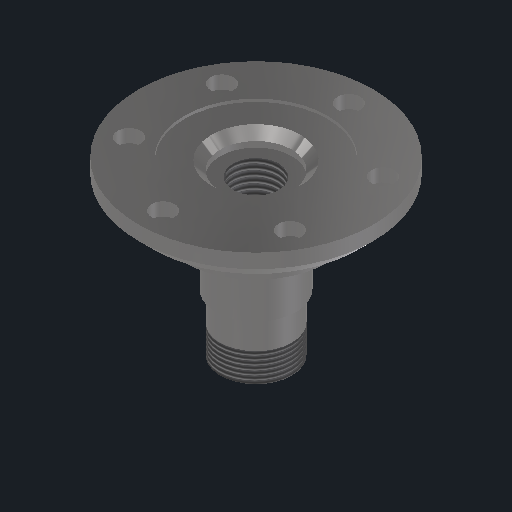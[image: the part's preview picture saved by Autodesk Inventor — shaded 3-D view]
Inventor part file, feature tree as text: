
AUTODESK INVENTOR PART (.ipt)
format: ipt  version: 2022 (Build 260153000, 153)  size: 221,184 bytes
history: native  units: mm
features: chamfer x4, sketch x3, other x3, thread x2, revolve x1, hole x1, extrude x1, reference x1, projected_geometry x1
ambient origin geometry x8: Origin, YZ Plane, XZ Plane, XY Plane, X Axis, Y Axis, Z Axis, Center Point
bodies: Solid1 (feature_tree)
feature tree (17):
  revolve  "Revolution1"  [1 undecoded]
  thread  "Thread1"  [1 undecoded]
  chamfer  "Chamfer1"  Distance=44.0mm
  chamfer  "Chamfer2"  Distance=25.0mm
  hole  "Hole1"  [1 undecoded]
  chamfer  "Chamfer4"  Distance=1.0mm
  extrude  "Extrusion1"  Depth=6.0mm
  chamfer  "Chamfer5"  Distance=5.0mm Angle=45.0deg
  thread  "Thread2"  [1 undecoded]
  sketch  "Sketch1"  dims[d3=28.0mm d4=50.0mm d7=360.0deg d8=44.0mm d9=0.0mm]
  sketch  "Sketch2"  dims[d10=16.0mm]
  reference  "Reference1"
  sketch  "Sketch3"  dims[d11=82.0mm d13=25.0mm d14=50.0mm d15=1.0mm d16=6.0mm d17=5.0mm d18=2.0mm d19=45.0deg d21=10.0mm d23=50.0mm d24=5.0mm d25=2.0mm d26=45.0deg d30=65.0mm d31=60.0mm d33=360.0deg d35=4.5mm d36=6.0mm d37=8.0mm d38=4.6mm d39=14.3117mm d40=12.0mm d41=20.594885mm d42=3.0mm d43=2.0mm d44=30.0deg d45=25.0mm d46=20.0mm d47=0.0mm d48=20.0mm d49=2.0mm d50=2.0mm d51=45.0deg d52=10.0mm d53=0.0mm d54=10.0mm d55=0.872665mm]
  projected_geometry  "Projected Loop1"
  other  "SistemaDeElevación.iam"
  other  "Bearing:2"
  other  "ISO 104 (Single Direction) 1 11 - 30 x 47 x 11:1"
note: 4 required parameter values undecoded (feature->parameter linkage not recoverable at this tier; creation-order binding heuristic only, values carry confidence <= 0.55)